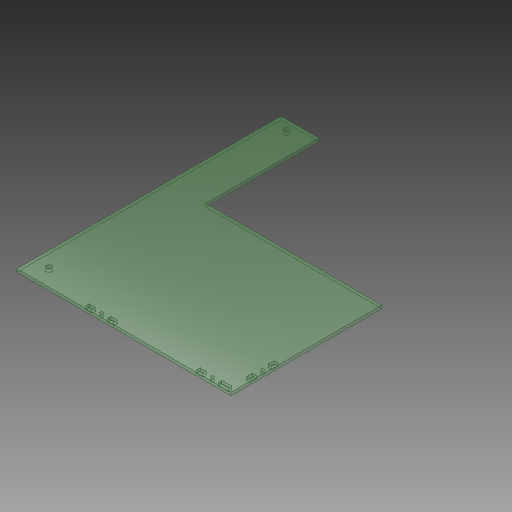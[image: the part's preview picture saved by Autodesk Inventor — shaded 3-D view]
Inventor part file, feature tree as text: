
AUTODESK INVENTOR PART (.ipt)
format: ipt  version: 2018 (Build 220112000, 112)  size: 471,552 bytes
history: native  units: mm
features: sketch x7, extrude x5, hole x2, projected_geometry x1
ambient origin geometry x8: Origin, YZ Plane, XZ Plane, XY Plane, X Axis, Y Axis, Z Axis, Center Point
bodies: Solid1 (feature_tree)
feature tree (15):
  extrude  "Extrusion1"  Depth=3.0mm TaperAngle=0.0deg
  hole  "Hole1"  [1 undecoded]
  hole  "Hole2"  [1 undecoded]
  extrude  "Extrusion2"  [1 undecoded]
  extrude  "Extrusion3"  [1 undecoded]
  extrude  "Extrusion4"  [1 undecoded]
  extrude  "Extrusion5"  [1 undecoded]
  sketch  "Sketch1"  dims[d0=3.0mm d1=0.0mm]
  sketch  "Sketch2"  dims[d2=3.2mm d3=6.0mm d4=4.0mm d5=2.0mm d6=90.0deg d7=8.0mm d8=20.594885mm]
  projected_geometry  "Projected Loop1"
  sketch  "Sketch5"  dims[d9=5.2mm d10=6.0mm d11=4.0mm d12=2.0mm d13=90.0deg d14=8.0mm d15=20.594885mm d16=3.0mm d17=0.0mm]
  sketch  "Sketch6"  dims[d18=5.2mm d19=3.0mm d20=0.0mm]
  sketch  "Sketch7"  dims[d21=3.0mm d22=0.0mm d23=0.0mm d24=0.0mm]
  sketch  "Sketch8"
  sketch  "Sketch9"
note: 6 required parameter values undecoded (feature->parameter linkage not recoverable at this tier; creation-order binding heuristic only, values carry confidence <= 0.55)
